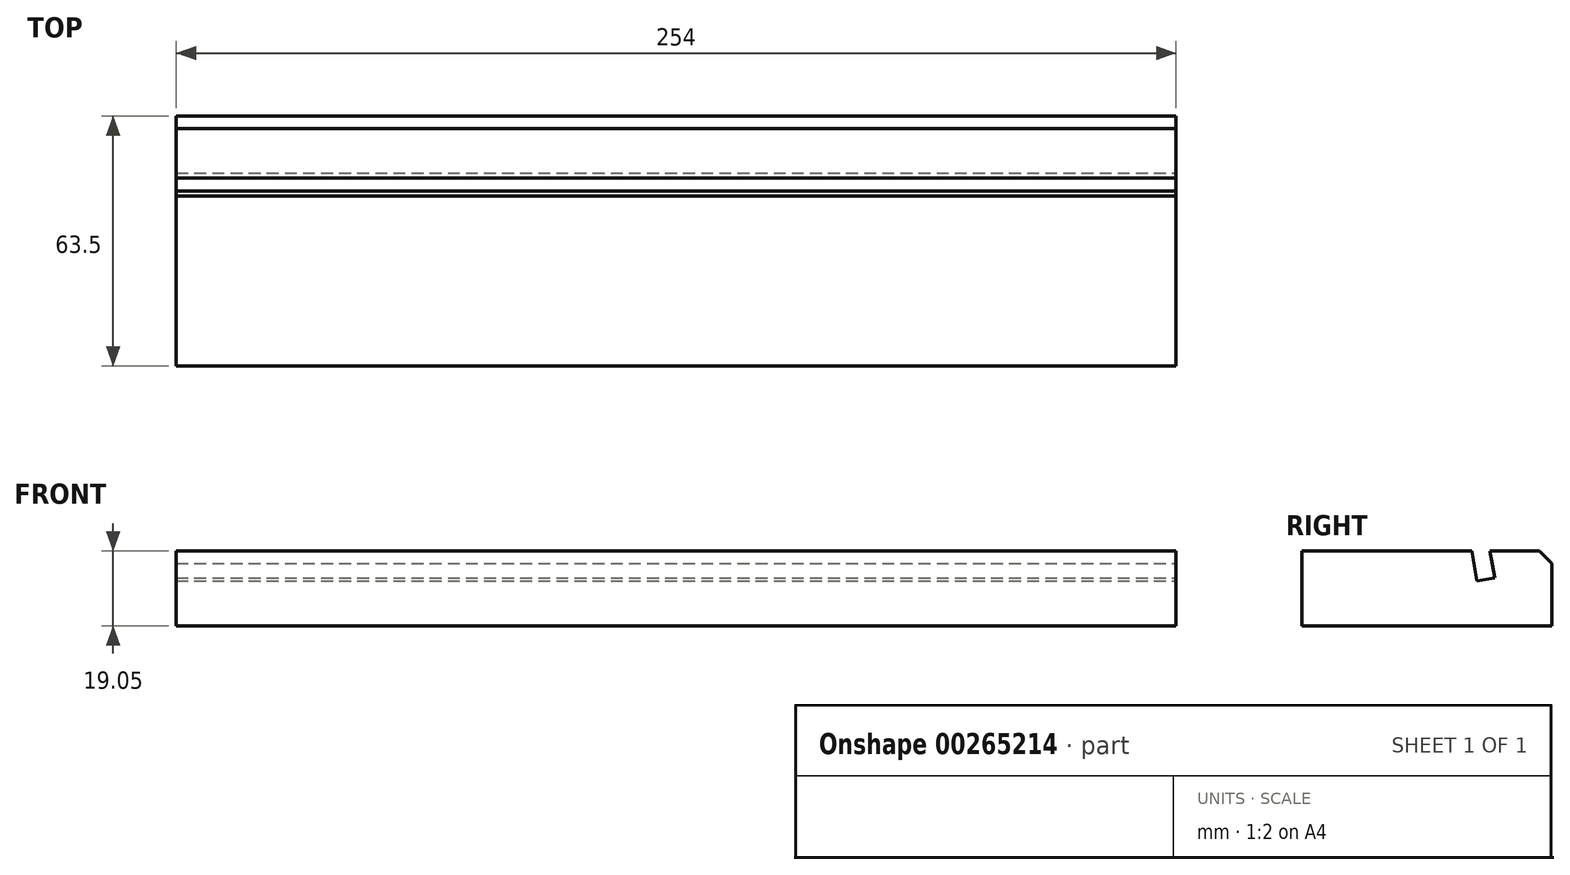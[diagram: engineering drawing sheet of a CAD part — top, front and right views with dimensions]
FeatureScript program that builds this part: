
annotation { "Feature Type Name" : "Feature", "Feature Type Description" : "" }
export const myFeature = defineFeature(function(context is Context, id is Id, definition is map)
    precondition{}
    {
        {
            var Q0;
            Q0=qCreatedBy(makeId("Right.planeOp"),FACE);
            var sketch = newSketch(context, id + "F0", { "sketchPlane" : qUnion([Q0])});
            skLineSegment(sketch, "E0.bottom", {"start": v(0, 0) * mm, "end": v(63.5, 0) * mm});
            skLineSegment(sketch, "E0.top", {"start": v(0, 19.05) * mm, "end": v(63.5, 19.05) * mm});
            skLineSegment(sketch, "E0.left", {"start": v(0, 0) * mm, "end": v(0, 19.05) * mm});
            skLineSegment(sketch, "E0.right", {"start": v(63.5, 0) * mm, "end": v(63.5, 19.05) * mm});
            skSolve(sketch);
        }
        {
            var Q0;
            Q0 = qSketchRegion(id + "F0", true);
            extrude(context, id + "F1", {"entities" : qUnion([Q0]), "depth" : 254 * mm});
        }
        {
            var Q0;
            Q0=makeQuery(id+"F1.opExtrude","SWEPT_EDGE",EDGE,{"disambiguationData":[OSD([sQuery(id+"F0.wireOp",EDGE,"E0.top"),sQuery(id+"F0.wireOp",EDGE,"E0.right")])]});
            chamfer(context, id + "F2", {"entities" : qUnion([Q0]), "width" : 3.17 * mm, "tangentPropagation" : true});
        }
        {
            var Q0;
            Q0=makeQuery(id+"F1.opExtrude","CAP_FACE",FACE,{"disambiguationData":[OSD([sQuery(id+"F0.wireOp",EDGE,"E0.bottom"),sQuery(id+"F0.wireOp",EDGE,"E0.top"),sQuery(id+"F0.wireOp",EDGE,"E0.left"),sQuery(id+"F0.wireOp",EDGE,"E0.right")])],"isStart":false});
            var sketch = newSketch(context, id + "F3", { "sketchPlane" : qUnion([Q0])});
            skLineSegment(sketch, "E1.bottom", {"start": v(41.39, 28.8) * mm, "end": v(45.89, 29.6) * mm});
            skLineSegment(sketch, "E1.top", {"start": v(44.45, 11.43) * mm, "end": v(48.95, 12.22) * mm});
            skLineSegment(sketch, "E1.left", {"start": v(41.39, 28.8) * mm, "end": v(44.45, 11.43) * mm});
            skLineSegment(sketch, "E1.right", {"start": v(45.89, 29.6) * mm, "end": v(48.95, 12.22) * mm});
            skSolve(sketch);
        }
        {
            var Q0;
            Q0 = qSketchRegion(id + "F3", true);
            extrude(context, id + "F4", {"entities" : qUnion([Q0]), "operationType" : NewBodyOperationType.REMOVE, "endBound" : BoundingType.THROUGH_ALL, "oppositeDirection" : true, "depth" : 25.4 * mm});
        }
        {
            var Q0;
            Q0=makeQuery(id+"F1.opExtrude","SWEPT_BODY",BODY,{"disambiguationData":[OSD([sQuery(id+"F0.wireOp",EDGE,"E0.bottom"),sQuery(id+"F0.wireOp",EDGE,"E0.top"),sQuery(id+"F0.wireOp",EDGE,"E0.left"),sQuery(id+"F0.wireOp",EDGE,"E0.right")])]});
            transform(context, id + "F5", {"entities" : qUnion([Q0]), "transformType" : TransformType.TRANSLATION_3D, "dx" : 0 * mm, "dy" : 0 * mm, "dz" : 82.55 * mm, "makeCopy" : true});
        }
        {
            var Q0;
            Q0=makeQuery(id+"F1.opExtrude","SWEPT_BODY",BODY,{"disambiguationData":[OSD([sQuery(id+"F0.wireOp",EDGE,"E0.bottom"),sQuery(id+"F0.wireOp",EDGE,"E0.top"),sQuery(id+"F0.wireOp",EDGE,"E0.left"),sQuery(id+"F0.wireOp",EDGE,"E0.right")])]});
            transform(context, id + "F6", {"entities" : qUnion([Q0]), "transformType" : TransformType.TRANSLATION_3D, "dx" : 0 * mm, "dy" : 0 * mm, "dz" : 165.1 * mm, "makeCopy" : true});
        }
        {
            var Q0;
            Q0=makeQuery(id+"F1.opExtrude","SWEPT_BODY",BODY,{"disambiguationData":[OSD([sQuery(id+"F0.wireOp",EDGE,"E0.bottom"),sQuery(id+"F0.wireOp",EDGE,"E0.top"),sQuery(id+"F0.wireOp",EDGE,"E0.left"),sQuery(id+"F0.wireOp",EDGE,"E0.right")])]});
            transform(context, id + "F7", {"entities" : qUnion([Q0]), "transformType" : TransformType.TRANSLATION_3D, "dx" : 0 * mm, "dy" : 0 * mm, "dz" : 247.65 * mm, "makeCopy" : true});
        }
        {
            var Q0;
            Q0=makeQuery(id+"F5.opPattern","COPY",BODY,{"derivedFrom":makeQuery(id+"F1.opExtrude","SWEPT_BODY",BODY,{"disambiguationData":[OSD([sQuery(id+"F0.wireOp",EDGE,"E0.bottom"),sQuery(id+"F0.wireOp",EDGE,"E0.top"),sQuery(id+"F0.wireOp",EDGE,"E0.left"),sQuery(id+"F0.wireOp",EDGE,"E0.right")])]}),"instanceName":"1"});
            var Q1;
            Q1=makeQuery(id+"F6.opPattern","COPY",BODY,{"derivedFrom":makeQuery(id+"F1.opExtrude","SWEPT_BODY",BODY,{"disambiguationData":[OSD([sQuery(id+"F0.wireOp",EDGE,"E0.bottom"),sQuery(id+"F0.wireOp",EDGE,"E0.top"),sQuery(id+"F0.wireOp",EDGE,"E0.left"),sQuery(id+"F0.wireOp",EDGE,"E0.right")])]}),"instanceName":"1"});
            var Q2;
            Q2=makeQuery(id+"F7.opPattern","COPY",BODY,{"derivedFrom":makeQuery(id+"F1.opExtrude","SWEPT_BODY",BODY,{"disambiguationData":[OSD([sQuery(id+"F0.wireOp",EDGE,"E0.bottom"),sQuery(id+"F0.wireOp",EDGE,"E0.top"),sQuery(id+"F0.wireOp",EDGE,"E0.left"),sQuery(id+"F0.wireOp",EDGE,"E0.right")])]}),"instanceName":"1"});
            deleteBodies(context, id + "F8", {"entities" : qUnion([Q0, Q1, Q2])});
        }
    });
